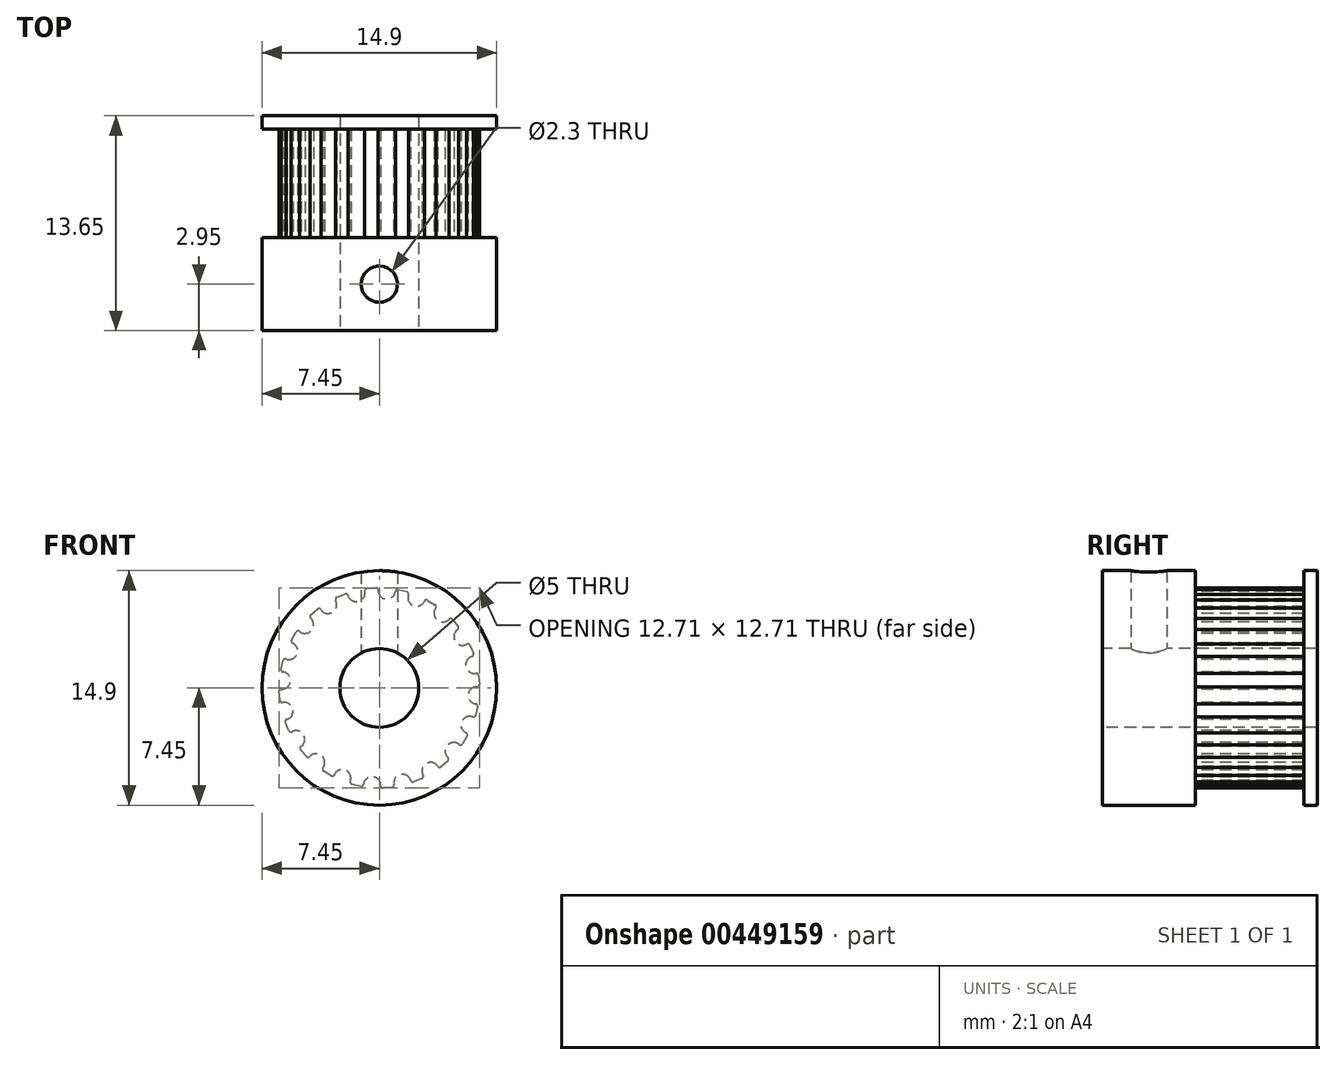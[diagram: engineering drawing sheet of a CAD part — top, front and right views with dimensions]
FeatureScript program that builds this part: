
annotation { "Feature Type Name" : "Feature", "Feature Type Description" : "" }
export const myFeature = defineFeature(function(context is Context, id is Id, definition is map)
    precondition{}
    {
        {
            var Q0;
            Q0=qCreatedBy(makeId("Front.planeOp"),FACE);
            var sketch = newSketch(context, id + "F0", { "sketchPlane" : qUnion([Q0])});
            skLineSegment(sketch, "E0", {"start": v(0, 0) * mm, "end": v(2.42, 5.89) * mm, "construction": true});
            skArc(sketch, "E1", {"start": v(0.43, 5.64) * mm, "mid": v(0.82, 5.76) * mm, "end": v(1.02, 6.12) * mm});
            skArc(sketch, "E2", {"start": v(1.84, 5.93) * mm, "mid": v(1.86, 5.52) * mm, "end": v(2.15, 5.23) * mm});
            skLineSegment(sketch, "E3", {"start": v(1.02, 6.13) * mm, "end": v(1.02, 6.12) * mm});
            skLineSegment(sketch, "E4", {"start": v(1.84, 5.94) * mm, "end": v(1.84, 5.93) * mm});
            skLineSegment(sketch, "E5", {"start": v(1.19, 6.25) * mm, "end": v(1.74, 6.11) * mm});
            skArc(sketch, "E6.filletArc", {"start": v(1.19, 6.25) * mm, "mid": v(1.08, 6.23) * mm, "end": v(1.02, 6.13) * mm});
            skArc(sketch, "E7.filletArc", {"start": v(1.84, 5.94) * mm, "mid": v(1.83, 6.05) * mm, "end": v(1.74, 6.11) * mm});
            skArc(sketch, "E8.1.0", {"start": v(-1.34, 5.5) * mm, "mid": v(-1, 5.73) * mm, "end": v(-0.93, 6.14) * mm});
            skArc(sketch, "E8.1.1", {"start": v(-0.8, 6.3) * mm, "mid": v(-0.9, 6.25) * mm, "end": v(-0.93, 6.15) * mm});
            skLineSegment(sketch, "E8.1.2", {"start": v(-0.8, 6.3) * mm, "end": v(-0.23, 6.35) * mm});
            skLineSegment(sketch, "E8.1.3", {"start": v(-0.93, 6.15) * mm, "end": v(-0.93, 6.14) * mm});
            skArc(sketch, "E8.1.4", {"start": v(-0.08, 6.22) * mm, "mid": v(-0.13, 6.32) * mm, "end": v(-0.23, 6.35) * mm});
            skLineSegment(sketch, "E8.1.5", {"start": v(-0.08, 6.22) * mm, "end": v(-0.08, 6.2) * mm});
            skArc(sketch, "E8.1.6", {"start": v(-0.08, 6.2) * mm, "mid": v(0.06, 5.82) * mm, "end": v(0.43, 5.64) * mm});
            skArc(sketch, "E8.2.0", {"start": v(-2.97, 4.81) * mm, "mid": v(-2.73, 5.14) * mm, "end": v(-2.78, 5.55) * mm});
            skArc(sketch, "E8.2.1", {"start": v(-2.71, 5.75) * mm, "mid": v(-2.79, 5.67) * mm, "end": v(-2.78, 5.56) * mm});
            skLineSegment(sketch, "E8.2.2", {"start": v(-2.71, 5.75) * mm, "end": v(-2.18, 5.97) * mm});
            skLineSegment(sketch, "E8.2.3", {"start": v(-2.78, 5.56) * mm, "end": v(-2.78, 5.55) * mm});
            skArc(sketch, "E8.2.4", {"start": v(-2, 5.89) * mm, "mid": v(-2.07, 5.97) * mm, "end": v(-2.18, 5.97) * mm});
            skLineSegment(sketch, "E8.2.5", {"start": v(-2, 5.89) * mm, "end": v(-2, 5.88) * mm});
            skArc(sketch, "E8.2.6", {"start": v(-2, 5.88) * mm, "mid": v(-1.74, 5.55) * mm, "end": v(-1.34, 5.5) * mm});
            skArc(sketch, "E8.3.0", {"start": v(-4.31, 3.66) * mm, "mid": v(-4.18, 4.05) * mm, "end": v(-4.36, 4.42) * mm});
            skArc(sketch, "E8.3.1", {"start": v(-4.35, 4.63) * mm, "mid": v(-4.4, 4.53) * mm, "end": v(-4.36, 4.43) * mm});
            skLineSegment(sketch, "E8.3.2", {"start": v(-4.35, 4.63) * mm, "end": v(-3.92, 5) * mm});
            skLineSegment(sketch, "E8.3.3", {"start": v(-4.36, 4.43) * mm, "end": v(-4.36, 4.42) * mm});
            skArc(sketch, "E8.3.4", {"start": v(-3.72, 4.98) * mm, "mid": v(-3.82, 5.04) * mm, "end": v(-3.92, 5) * mm});
            skLineSegment(sketch, "E8.3.5", {"start": v(-3.72, 4.98) * mm, "end": v(-3.71, 4.97) * mm});
            skArc(sketch, "E8.3.6", {"start": v(-3.71, 4.97) * mm, "mid": v(-3.37, 4.74) * mm, "end": v(-2.97, 4.81) * mm});
            skArc(sketch, "E8.4.0", {"start": v(-5.23, 2.15) * mm, "mid": v(-5.23, 2.56) * mm, "end": v(-5.5, 2.86) * mm});
            skArc(sketch, "E8.4.1", {"start": v(-5.57, 3.06) * mm, "mid": v(-5.59, 2.95) * mm, "end": v(-5.52, 2.86) * mm});
            skLineSegment(sketch, "E8.4.2", {"start": v(-5.57, 3.06) * mm, "end": v(-5.28, 3.55) * mm});
            skLineSegment(sketch, "E8.4.3", {"start": v(-5.52, 2.86) * mm, "end": v(-5.5, 2.86) * mm});
            skArc(sketch, "E8.4.4", {"start": v(-5.08, 3.59) * mm, "mid": v(-5.19, 3.61) * mm, "end": v(-5.28, 3.55) * mm});
            skLineSegment(sketch, "E8.4.5", {"start": v(-5.08, 3.59) * mm, "end": v(-5.07, 3.58) * mm});
            skArc(sketch, "E8.4.6", {"start": v(-5.07, 3.58) * mm, "mid": v(-4.67, 3.47) * mm, "end": v(-4.31, 3.66) * mm});
            skArc(sketch, "E8.5.0", {"start": v(-5.64, 0.43) * mm, "mid": v(-5.76, 0.82) * mm, "end": v(-6.12, 1.02) * mm});
            skArc(sketch, "E8.5.1", {"start": v(-6.25, 1.19) * mm, "mid": v(-6.23, 1.08) * mm, "end": v(-6.13, 1.02) * mm});
            skLineSegment(sketch, "E8.5.2", {"start": v(-6.25, 1.19) * mm, "end": v(-6.11, 1.74) * mm});
            skLineSegment(sketch, "E8.5.3", {"start": v(-6.13, 1.02) * mm, "end": v(-6.12, 1.02) * mm});
            skArc(sketch, "E8.5.4", {"start": v(-5.94, 1.84) * mm, "mid": v(-6.05, 1.83) * mm, "end": v(-6.11, 1.74) * mm});
            skLineSegment(sketch, "E8.5.5", {"start": v(-5.94, 1.84) * mm, "end": v(-5.93, 1.84) * mm});
            skArc(sketch, "E8.5.6", {"start": v(-5.93, 1.84) * mm, "mid": v(-5.52, 1.86) * mm, "end": v(-5.23, 2.15) * mm});
            skArc(sketch, "E8.6.0", {"start": v(-5.5, -1.34) * mm, "mid": v(-5.73, -1) * mm, "end": v(-6.14, -0.93) * mm});
            skArc(sketch, "E8.6.1", {"start": v(-6.3, -0.8) * mm, "mid": v(-6.25, -0.9) * mm, "end": v(-6.15, -0.93) * mm});
            skLineSegment(sketch, "E8.6.2", {"start": v(-6.3, -0.8) * mm, "end": v(-6.35, -0.23) * mm});
            skLineSegment(sketch, "E8.6.3", {"start": v(-6.15, -0.93) * mm, "end": v(-6.14, -0.93) * mm});
            skArc(sketch, "E8.6.4", {"start": v(-6.22, -0.08) * mm, "mid": v(-6.32, -0.13) * mm, "end": v(-6.35, -0.23) * mm});
            skLineSegment(sketch, "E8.6.5", {"start": v(-6.22, -0.08) * mm, "end": v(-6.2, -0.08) * mm});
            skArc(sketch, "E8.6.6", {"start": v(-6.2, -0.08) * mm, "mid": v(-5.82, 0.06) * mm, "end": v(-5.64, 0.43) * mm});
            skArc(sketch, "E8.7.0", {"start": v(-4.81, -2.97) * mm, "mid": v(-5.14, -2.73) * mm, "end": v(-5.55, -2.78) * mm});
            skArc(sketch, "E8.7.1", {"start": v(-5.75, -2.71) * mm, "mid": v(-5.67, -2.79) * mm, "end": v(-5.56, -2.78) * mm});
            skLineSegment(sketch, "E8.7.2", {"start": v(-5.75, -2.71) * mm, "end": v(-5.97, -2.18) * mm});
            skLineSegment(sketch, "E8.7.3", {"start": v(-5.56, -2.78) * mm, "end": v(-5.55, -2.78) * mm});
            skArc(sketch, "E8.7.4", {"start": v(-5.89, -2) * mm, "mid": v(-5.97, -2.07) * mm, "end": v(-5.97, -2.18) * mm});
            skLineSegment(sketch, "E8.7.5", {"start": v(-5.89, -2) * mm, "end": v(-5.88, -2) * mm});
            skArc(sketch, "E8.7.6", {"start": v(-5.88, -2) * mm, "mid": v(-5.55, -1.74) * mm, "end": v(-5.5, -1.34) * mm});
            skArc(sketch, "E8.8.0", {"start": v(-3.66, -4.31) * mm, "mid": v(-4.05, -4.18) * mm, "end": v(-4.42, -4.36) * mm});
            skArc(sketch, "E8.8.1", {"start": v(-4.63, -4.35) * mm, "mid": v(-4.53, -4.4) * mm, "end": v(-4.43, -4.36) * mm});
            skLineSegment(sketch, "E8.8.2", {"start": v(-4.63, -4.35) * mm, "end": v(-5, -3.92) * mm});
            skLineSegment(sketch, "E8.8.3", {"start": v(-4.43, -4.36) * mm, "end": v(-4.42, -4.36) * mm});
            skArc(sketch, "E8.8.4", {"start": v(-4.98, -3.72) * mm, "mid": v(-5.04, -3.82) * mm, "end": v(-5, -3.92) * mm});
            skLineSegment(sketch, "E8.8.5", {"start": v(-4.98, -3.72) * mm, "end": v(-4.97, -3.71) * mm});
            skArc(sketch, "E8.8.6", {"start": v(-4.97, -3.71) * mm, "mid": v(-4.74, -3.37) * mm, "end": v(-4.81, -2.97) * mm});
            skArc(sketch, "E8.9.0", {"start": v(-2.15, -5.23) * mm, "mid": v(-2.56, -5.23) * mm, "end": v(-2.86, -5.5) * mm});
            skArc(sketch, "E8.9.1", {"start": v(-3.06, -5.57) * mm, "mid": v(-2.95, -5.59) * mm, "end": v(-2.86, -5.52) * mm});
            skLineSegment(sketch, "E8.9.2", {"start": v(-3.06, -5.57) * mm, "end": v(-3.55, -5.28) * mm});
            skLineSegment(sketch, "E8.9.3", {"start": v(-2.86, -5.52) * mm, "end": v(-2.86, -5.5) * mm});
            skArc(sketch, "E8.9.4", {"start": v(-3.59, -5.08) * mm, "mid": v(-3.61, -5.19) * mm, "end": v(-3.55, -5.28) * mm});
            skLineSegment(sketch, "E8.9.5", {"start": v(-3.59, -5.08) * mm, "end": v(-3.58, -5.07) * mm});
            skArc(sketch, "E8.9.6", {"start": v(-3.58, -5.07) * mm, "mid": v(-3.47, -4.67) * mm, "end": v(-3.66, -4.31) * mm});
            skArc(sketch, "E8.10.0", {"start": v(-0.43, -5.64) * mm, "mid": v(-0.82, -5.76) * mm, "end": v(-1.02, -6.12) * mm});
            skArc(sketch, "E8.10.1", {"start": v(-1.19, -6.25) * mm, "mid": v(-1.08, -6.23) * mm, "end": v(-1.02, -6.13) * mm});
            skLineSegment(sketch, "E8.10.2", {"start": v(-1.19, -6.25) * mm, "end": v(-1.74, -6.11) * mm});
            skLineSegment(sketch, "E8.10.3", {"start": v(-1.02, -6.13) * mm, "end": v(-1.02, -6.12) * mm});
            skArc(sketch, "E8.10.4", {"start": v(-1.84, -5.94) * mm, "mid": v(-1.83, -6.05) * mm, "end": v(-1.74, -6.11) * mm});
            skLineSegment(sketch, "E8.10.5", {"start": v(-1.84, -5.94) * mm, "end": v(-1.84, -5.93) * mm});
            skArc(sketch, "E8.10.6", {"start": v(-1.84, -5.93) * mm, "mid": v(-1.86, -5.52) * mm, "end": v(-2.15, -5.23) * mm});
            skArc(sketch, "E8.11.0", {"start": v(1.34, -5.5) * mm, "mid": v(1, -5.73) * mm, "end": v(0.93, -6.14) * mm});
            skArc(sketch, "E8.11.1", {"start": v(0.8, -6.3) * mm, "mid": v(0.9, -6.25) * mm, "end": v(0.93, -6.15) * mm});
            skLineSegment(sketch, "E8.11.2", {"start": v(0.8, -6.3) * mm, "end": v(0.23, -6.35) * mm});
            skLineSegment(sketch, "E8.11.3", {"start": v(0.93, -6.15) * mm, "end": v(0.93, -6.14) * mm});
            skArc(sketch, "E8.11.4", {"start": v(0.08, -6.22) * mm, "mid": v(0.13, -6.32) * mm, "end": v(0.23, -6.35) * mm});
            skLineSegment(sketch, "E8.11.5", {"start": v(0.08, -6.22) * mm, "end": v(0.08, -6.2) * mm});
            skArc(sketch, "E8.11.6", {"start": v(0.08, -6.2) * mm, "mid": v(-0.06, -5.82) * mm, "end": v(-0.43, -5.64) * mm});
            skArc(sketch, "E8.12.0", {"start": v(2.97, -4.81) * mm, "mid": v(2.73, -5.14) * mm, "end": v(2.78, -5.55) * mm});
            skArc(sketch, "E8.12.1", {"start": v(2.71, -5.75) * mm, "mid": v(2.79, -5.67) * mm, "end": v(2.78, -5.56) * mm});
            skLineSegment(sketch, "E8.12.2", {"start": v(2.71, -5.75) * mm, "end": v(2.18, -5.97) * mm});
            skLineSegment(sketch, "E8.12.3", {"start": v(2.78, -5.56) * mm, "end": v(2.78, -5.55) * mm});
            skArc(sketch, "E8.12.4", {"start": v(2, -5.89) * mm, "mid": v(2.07, -5.97) * mm, "end": v(2.18, -5.97) * mm});
            skLineSegment(sketch, "E8.12.5", {"start": v(2, -5.89) * mm, "end": v(2, -5.88) * mm});
            skArc(sketch, "E8.12.6", {"start": v(2, -5.88) * mm, "mid": v(1.74, -5.55) * mm, "end": v(1.34, -5.5) * mm});
            skArc(sketch, "E8.13.0", {"start": v(4.31, -3.66) * mm, "mid": v(4.18, -4.05) * mm, "end": v(4.36, -4.42) * mm});
            skArc(sketch, "E8.13.1", {"start": v(4.35, -4.63) * mm, "mid": v(4.4, -4.53) * mm, "end": v(4.36, -4.43) * mm});
            skLineSegment(sketch, "E8.13.2", {"start": v(4.35, -4.63) * mm, "end": v(3.92, -5) * mm});
            skLineSegment(sketch, "E8.13.3", {"start": v(4.36, -4.43) * mm, "end": v(4.36, -4.42) * mm});
            skArc(sketch, "E8.13.4", {"start": v(3.72, -4.98) * mm, "mid": v(3.82, -5.04) * mm, "end": v(3.92, -5) * mm});
            skLineSegment(sketch, "E8.13.5", {"start": v(3.72, -4.98) * mm, "end": v(3.71, -4.97) * mm});
            skArc(sketch, "E8.13.6", {"start": v(3.71, -4.97) * mm, "mid": v(3.37, -4.74) * mm, "end": v(2.97, -4.81) * mm});
            skArc(sketch, "E8.14.0", {"start": v(5.23, -2.15) * mm, "mid": v(5.23, -2.56) * mm, "end": v(5.5, -2.86) * mm});
            skArc(sketch, "E8.14.1", {"start": v(5.57, -3.06) * mm, "mid": v(5.59, -2.95) * mm, "end": v(5.52, -2.86) * mm});
            skLineSegment(sketch, "E8.14.2", {"start": v(5.57, -3.06) * mm, "end": v(5.28, -3.55) * mm});
            skLineSegment(sketch, "E8.14.3", {"start": v(5.52, -2.86) * mm, "end": v(5.5, -2.86) * mm});
            skArc(sketch, "E8.14.4", {"start": v(5.08, -3.59) * mm, "mid": v(5.19, -3.61) * mm, "end": v(5.28, -3.55) * mm});
            skLineSegment(sketch, "E8.14.5", {"start": v(5.08, -3.59) * mm, "end": v(5.07, -3.58) * mm});
            skArc(sketch, "E8.14.6", {"start": v(5.07, -3.58) * mm, "mid": v(4.67, -3.47) * mm, "end": v(4.31, -3.66) * mm});
            skArc(sketch, "E8.15.0", {"start": v(5.64, -0.43) * mm, "mid": v(5.76, -0.82) * mm, "end": v(6.12, -1.02) * mm});
            skArc(sketch, "E8.15.1", {"start": v(6.25, -1.19) * mm, "mid": v(6.23, -1.08) * mm, "end": v(6.13, -1.02) * mm});
            skLineSegment(sketch, "E8.15.2", {"start": v(6.25, -1.19) * mm, "end": v(6.11, -1.74) * mm});
            skLineSegment(sketch, "E8.15.3", {"start": v(6.13, -1.02) * mm, "end": v(6.12, -1.02) * mm});
            skArc(sketch, "E8.15.4", {"start": v(5.94, -1.84) * mm, "mid": v(6.05, -1.83) * mm, "end": v(6.11, -1.74) * mm});
            skLineSegment(sketch, "E8.15.5", {"start": v(5.94, -1.84) * mm, "end": v(5.93, -1.84) * mm});
            skArc(sketch, "E8.15.6", {"start": v(5.93, -1.84) * mm, "mid": v(5.52, -1.86) * mm, "end": v(5.23, -2.15) * mm});
            skArc(sketch, "E8.16.0", {"start": v(5.5, 1.34) * mm, "mid": v(5.73, 1) * mm, "end": v(6.14, 0.93) * mm});
            skArc(sketch, "E8.16.1", {"start": v(6.3, 0.8) * mm, "mid": v(6.25, 0.9) * mm, "end": v(6.15, 0.93) * mm});
            skLineSegment(sketch, "E8.16.2", {"start": v(6.3, 0.8) * mm, "end": v(6.35, 0.23) * mm});
            skLineSegment(sketch, "E8.16.3", {"start": v(6.15, 0.93) * mm, "end": v(6.14, 0.93) * mm});
            skArc(sketch, "E8.16.4", {"start": v(6.22, 0.08) * mm, "mid": v(6.32, 0.13) * mm, "end": v(6.35, 0.23) * mm});
            skLineSegment(sketch, "E8.16.5", {"start": v(6.22, 0.08) * mm, "end": v(6.2, 0.08) * mm});
            skArc(sketch, "E8.16.6", {"start": v(6.2, 0.08) * mm, "mid": v(5.82, -0.06) * mm, "end": v(5.64, -0.43) * mm});
            skArc(sketch, "E8.17.0", {"start": v(4.81, 2.97) * mm, "mid": v(5.14, 2.73) * mm, "end": v(5.55, 2.78) * mm});
            skArc(sketch, "E8.17.1", {"start": v(5.75, 2.71) * mm, "mid": v(5.67, 2.79) * mm, "end": v(5.56, 2.78) * mm});
            skLineSegment(sketch, "E8.17.2", {"start": v(5.75, 2.71) * mm, "end": v(5.97, 2.18) * mm});
            skLineSegment(sketch, "E8.17.3", {"start": v(5.56, 2.78) * mm, "end": v(5.55, 2.78) * mm});
            skArc(sketch, "E8.17.4", {"start": v(5.89, 2) * mm, "mid": v(5.97, 2.07) * mm, "end": v(5.97, 2.18) * mm});
            skLineSegment(sketch, "E8.17.5", {"start": v(5.89, 2) * mm, "end": v(5.88, 2) * mm});
            skArc(sketch, "E8.17.6", {"start": v(5.88, 2) * mm, "mid": v(5.55, 1.74) * mm, "end": v(5.5, 1.34) * mm});
            skArc(sketch, "E8.18.0", {"start": v(3.66, 4.31) * mm, "mid": v(4.05, 4.18) * mm, "end": v(4.42, 4.36) * mm});
            skArc(sketch, "E8.18.1", {"start": v(4.63, 4.35) * mm, "mid": v(4.53, 4.4) * mm, "end": v(4.43, 4.36) * mm});
            skLineSegment(sketch, "E8.18.2", {"start": v(4.63, 4.35) * mm, "end": v(5, 3.92) * mm});
            skLineSegment(sketch, "E8.18.3", {"start": v(4.43, 4.36) * mm, "end": v(4.42, 4.36) * mm});
            skArc(sketch, "E8.18.4", {"start": v(4.98, 3.72) * mm, "mid": v(5.04, 3.82) * mm, "end": v(5, 3.92) * mm});
            skLineSegment(sketch, "E8.18.5", {"start": v(4.98, 3.72) * mm, "end": v(4.97, 3.71) * mm});
            skArc(sketch, "E8.18.6", {"start": v(4.97, 3.71) * mm, "mid": v(4.74, 3.37) * mm, "end": v(4.81, 2.97) * mm});
            skArc(sketch, "E8.19.0", {"start": v(2.15, 5.23) * mm, "mid": v(2.56, 5.23) * mm, "end": v(2.86, 5.5) * mm});
            skArc(sketch, "E8.19.1", {"start": v(3.06, 5.57) * mm, "mid": v(2.95, 5.59) * mm, "end": v(2.86, 5.52) * mm});
            skLineSegment(sketch, "E8.19.2", {"start": v(3.06, 5.57) * mm, "end": v(3.55, 5.28) * mm});
            skLineSegment(sketch, "E8.19.3", {"start": v(2.86, 5.52) * mm, "end": v(2.86, 5.5) * mm});
            skArc(sketch, "E8.19.4", {"start": v(3.59, 5.08) * mm, "mid": v(3.61, 5.19) * mm, "end": v(3.55, 5.28) * mm});
            skLineSegment(sketch, "E8.19.5", {"start": v(3.59, 5.08) * mm, "end": v(3.58, 5.07) * mm});
            skArc(sketch, "E8.19.6", {"start": v(3.58, 5.07) * mm, "mid": v(3.47, 4.67) * mm, "end": v(3.66, 4.31) * mm});
            skPoint(sketch, "E8.center", {"position": v(0, 0) * mm});
            skCircle(sketch, "E9", {"center": v(0, 0) * mm, "radius": 2.5 * mm});
            skCircle(sketch, "E10", {"center": v(0, 0) * mm, "radius": 7.45 * mm});
            skSolve(sketch);
        }
        {
            var Q0;
            Q0=makeQuery(id+"F0.imprint","IMPRINT",FACE,{"disambiguationData":[TD([[makeQuery(id+"F0.imprint","IMPRINT",EDGE,{"derivedFrom":sQuery(id+"F0.wireOp",EDGE,"E1")}),-1.0]])]});
            extrude(context, id + "F1", {"entities" : qUnion([Q0]), "oppositeDirection" : true, "depth" : 6.9 * mm});
        }
        {
            var Q0;
            Q0=makeQuery(id+"F0.imprint","IMPRINT",FACE,{"disambiguationData":[TD([[makeQuery(id+"F0.imprint","IMPRINT",EDGE,{"derivedFrom":sQuery(id+"F0.wireOp",EDGE,"E1")}),-1.0]])]});
            var Q1;
            Q1=makeQuery(id+"F0.imprint","IMPRINT",FACE,{"disambiguationData":[TD([[makeQuery(id+"F0.imprint","IMPRINT",EDGE,{"derivedFrom":sQuery(id+"F0.wireOp",EDGE,"E1")}),1.0]])]});
            extrude(context, id + "F2", {"entities" : qUnion([Q0, Q1]), "operationType" : NewBodyOperationType.ADD, "depth" : 5.9 * mm});
        }
        {
            var Q0;
            Q0=makeQuery(id+"F1.opExtrude","CAP_FACE",FACE,{"disambiguationData":[OSD([sQuery(id+"F0.wireOp",EDGE,"E1"),sQuery(id+"F0.wireOp",EDGE,"E2"),sQuery(id+"F0.wireOp",EDGE,"E3"),sQuery(id+"F0.wireOp",EDGE,"E4"),sQuery(id+"F0.wireOp",EDGE,"E5"),sQuery(id+"F0.wireOp",EDGE,"E6.filletArc"),sQuery(id+"F0.wireOp",EDGE,"E7.filletArc"),sQuery(id+"F0.wireOp",EDGE,"E8.1.0"),sQuery(id+"F0.wireOp",EDGE,"E8.1.1"),sQuery(id+"F0.wireOp",EDGE,"E8.1.2"),sQuery(id+"F0.wireOp",EDGE,"E8.1.3"),sQuery(id+"F0.wireOp",EDGE,"E8.1.4"),sQuery(id+"F0.wireOp",EDGE,"E8.1.5"),sQuery(id+"F0.wireOp",EDGE,"E8.1.6"),sQuery(id+"F0.wireOp",EDGE,"E8.2.0"),sQuery(id+"F0.wireOp",EDGE,"E8.2.1"),sQuery(id+"F0.wireOp",EDGE,"E8.2.2"),sQuery(id+"F0.wireOp",EDGE,"E8.2.3"),sQuery(id+"F0.wireOp",EDGE,"E8.2.4"),sQuery(id+"F0.wireOp",EDGE,"E8.2.5"),sQuery(id+"F0.wireOp",EDGE,"E8.2.6"),sQuery(id+"F0.wireOp",EDGE,"E8.3.0"),sQuery(id+"F0.wireOp",EDGE,"E8.3.1"),sQuery(id+"F0.wireOp",EDGE,"E8.3.2"),sQuery(id+"F0.wireOp",EDGE,"E8.3.3"),sQuery(id+"F0.wireOp",EDGE,"E8.3.4"),sQuery(id+"F0.wireOp",EDGE,"E8.3.5"),sQuery(id+"F0.wireOp",EDGE,"E8.3.6"),sQuery(id+"F0.wireOp",EDGE,"E8.4.0"),sQuery(id+"F0.wireOp",EDGE,"E8.4.1"),sQuery(id+"F0.wireOp",EDGE,"E8.4.2"),sQuery(id+"F0.wireOp",EDGE,"E8.4.3"),sQuery(id+"F0.wireOp",EDGE,"E8.4.4"),sQuery(id+"F0.wireOp",EDGE,"E8.4.5"),sQuery(id+"F0.wireOp",EDGE,"E8.4.6"),sQuery(id+"F0.wireOp",EDGE,"E8.5.0"),sQuery(id+"F0.wireOp",EDGE,"E8.5.1"),sQuery(id+"F0.wireOp",EDGE,"E8.5.2"),sQuery(id+"F0.wireOp",EDGE,"E8.5.3"),sQuery(id+"F0.wireOp",EDGE,"E8.5.4"),sQuery(id+"F0.wireOp",EDGE,"E8.5.5"),sQuery(id+"F0.wireOp",EDGE,"E8.5.6"),sQuery(id+"F0.wireOp",EDGE,"E8.6.0"),sQuery(id+"F0.wireOp",EDGE,"E8.6.1"),sQuery(id+"F0.wireOp",EDGE,"E8.6.2"),sQuery(id+"F0.wireOp",EDGE,"E8.6.3"),sQuery(id+"F0.wireOp",EDGE,"E8.6.4"),sQuery(id+"F0.wireOp",EDGE,"E8.6.5"),sQuery(id+"F0.wireOp",EDGE,"E8.6.6"),sQuery(id+"F0.wireOp",EDGE,"E8.7.0"),sQuery(id+"F0.wireOp",EDGE,"E8.7.1"),sQuery(id+"F0.wireOp",EDGE,"E8.7.2"),sQuery(id+"F0.wireOp",EDGE,"E8.7.3"),sQuery(id+"F0.wireOp",EDGE,"E8.7.4"),sQuery(id+"F0.wireOp",EDGE,"E8.7.5"),sQuery(id+"F0.wireOp",EDGE,"E8.7.6"),sQuery(id+"F0.wireOp",EDGE,"E8.8.0"),sQuery(id+"F0.wireOp",EDGE,"E8.8.1"),sQuery(id+"F0.wireOp",EDGE,"E8.8.2"),sQuery(id+"F0.wireOp",EDGE,"E8.8.3"),sQuery(id+"F0.wireOp",EDGE,"E8.8.4"),sQuery(id+"F0.wireOp",EDGE,"E8.8.5"),sQuery(id+"F0.wireOp",EDGE,"E8.8.6"),sQuery(id+"F0.wireOp",EDGE,"E8.9.0"),sQuery(id+"F0.wireOp",EDGE,"E8.9.1"),sQuery(id+"F0.wireOp",EDGE,"E8.9.2"),sQuery(id+"F0.wireOp",EDGE,"E8.9.3"),sQuery(id+"F0.wireOp",EDGE,"E8.9.4"),sQuery(id+"F0.wireOp",EDGE,"E8.9.5"),sQuery(id+"F0.wireOp",EDGE,"E8.9.6"),sQuery(id+"F0.wireOp",EDGE,"E8.10.0"),sQuery(id+"F0.wireOp",EDGE,"E8.10.1"),sQuery(id+"F0.wireOp",EDGE,"E8.10.2"),sQuery(id+"F0.wireOp",EDGE,"E8.10.3"),sQuery(id+"F0.wireOp",EDGE,"E8.10.4"),sQuery(id+"F0.wireOp",EDGE,"E8.10.5"),sQuery(id+"F0.wireOp",EDGE,"E8.10.6"),sQuery(id+"F0.wireOp",EDGE,"E8.11.0"),sQuery(id+"F0.wireOp",EDGE,"E8.11.1"),sQuery(id+"F0.wireOp",EDGE,"E8.11.2"),sQuery(id+"F0.wireOp",EDGE,"E8.11.3"),sQuery(id+"F0.wireOp",EDGE,"E8.11.4"),sQuery(id+"F0.wireOp",EDGE,"E8.11.5"),sQuery(id+"F0.wireOp",EDGE,"E8.11.6"),sQuery(id+"F0.wireOp",EDGE,"E8.12.0"),sQuery(id+"F0.wireOp",EDGE,"E8.12.1"),sQuery(id+"F0.wireOp",EDGE,"E8.12.2"),sQuery(id+"F0.wireOp",EDGE,"E8.12.3"),sQuery(id+"F0.wireOp",EDGE,"E8.12.4"),sQuery(id+"F0.wireOp",EDGE,"E8.12.5"),sQuery(id+"F0.wireOp",EDGE,"E8.12.6"),sQuery(id+"F0.wireOp",EDGE,"E8.13.0"),sQuery(id+"F0.wireOp",EDGE,"E8.13.1"),sQuery(id+"F0.wireOp",EDGE,"E8.13.2"),sQuery(id+"F0.wireOp",EDGE,"E8.13.3"),sQuery(id+"F0.wireOp",EDGE,"E8.13.4"),sQuery(id+"F0.wireOp",EDGE,"E8.13.5"),sQuery(id+"F0.wireOp",EDGE,"E8.13.6"),sQuery(id+"F0.wireOp",EDGE,"E8.14.0"),sQuery(id+"F0.wireOp",EDGE,"E8.14.1"),sQuery(id+"F0.wireOp",EDGE,"E8.14.2"),sQuery(id+"F0.wireOp",EDGE,"E8.14.3"),sQuery(id+"F0.wireOp",EDGE,"E8.14.4"),sQuery(id+"F0.wireOp",EDGE,"E8.14.5"),sQuery(id+"F0.wireOp",EDGE,"E8.14.6"),sQuery(id+"F0.wireOp",EDGE,"E8.15.0"),sQuery(id+"F0.wireOp",EDGE,"E8.15.1"),sQuery(id+"F0.wireOp",EDGE,"E8.15.2"),sQuery(id+"F0.wireOp",EDGE,"E8.15.3"),sQuery(id+"F0.wireOp",EDGE,"E8.15.4"),sQuery(id+"F0.wireOp",EDGE,"E8.15.5"),sQuery(id+"F0.wireOp",EDGE,"E8.15.6"),sQuery(id+"F0.wireOp",EDGE,"E8.16.0"),sQuery(id+"F0.wireOp",EDGE,"E8.16.1"),sQuery(id+"F0.wireOp",EDGE,"E8.16.2"),sQuery(id+"F0.wireOp",EDGE,"E8.16.3"),sQuery(id+"F0.wireOp",EDGE,"E8.16.4"),sQuery(id+"F0.wireOp",EDGE,"E8.16.5"),sQuery(id+"F0.wireOp",EDGE,"E8.16.6"),sQuery(id+"F0.wireOp",EDGE,"E8.17.0"),sQuery(id+"F0.wireOp",EDGE,"E8.17.1"),sQuery(id+"F0.wireOp",EDGE,"E8.17.2"),sQuery(id+"F0.wireOp",EDGE,"E8.17.3"),sQuery(id+"F0.wireOp",EDGE,"E8.17.4"),sQuery(id+"F0.wireOp",EDGE,"E8.17.5"),sQuery(id+"F0.wireOp",EDGE,"E8.17.6"),sQuery(id+"F0.wireOp",EDGE,"E8.18.0"),sQuery(id+"F0.wireOp",EDGE,"E8.18.1"),sQuery(id+"F0.wireOp",EDGE,"E8.18.2"),sQuery(id+"F0.wireOp",EDGE,"E8.18.3"),sQuery(id+"F0.wireOp",EDGE,"E8.18.4"),sQuery(id+"F0.wireOp",EDGE,"E8.18.5"),sQuery(id+"F0.wireOp",EDGE,"E8.18.6"),sQuery(id+"F0.wireOp",EDGE,"E8.19.0"),sQuery(id+"F0.wireOp",EDGE,"E8.19.1"),sQuery(id+"F0.wireOp",EDGE,"E8.19.2"),sQuery(id+"F0.wireOp",EDGE,"E8.19.3"),sQuery(id+"F0.wireOp",EDGE,"E8.19.4"),sQuery(id+"F0.wireOp",EDGE,"E8.19.5"),sQuery(id+"F0.wireOp",EDGE,"E8.19.6"),sQuery(id+"F0.wireOp",EDGE,"E9")])],"isStart":false});
            var sketch = newSketch(context, id + "F3", { "sketchPlane" : qUnion([Q0])});
            skCircle(sketch, "E11.0", {"center": v(0, 0) * mm, "radius": 7.45 * mm});
            skCircle(sketch, "E12.0", {"center": v(0, 0) * mm, "radius": 2.5 * mm});
            skSolve(sketch);
        }
        {
            var Q0;
            Q0=qSketchRegion(id+"F3",true);
            extrude(context, id + "F4", {"entities" : qUnion([Q0]), "operationType" : NewBodyOperationType.ADD, "depth" : .85 * mm});
        }
        {
            var Q0;
            Q0=qCreatedBy(makeId("Top.planeOp"),FACE);
            var sketch = newSketch(context, id + "F5", { "sketchPlane" : qUnion([Q0])});
            skLineSegment(sketch, "E13.0", {"start": v(2.5, -5.9) * mm, "end": v(-2.5, -5.9) * mm, "construction": true});
            skLineSegment(sketch, "E14.0.0", {"start": v(2.5, 0) * mm, "end": v(-2.5, 0) * mm, "construction": true});
            skLineSegment(sketch, "E15", {"start": v(0, -5.9) * mm, "end": v(0, 0) * mm, "construction": true});
            skCircle(sketch, "E16", {"center": v(0, -2.95) * mm, "radius": 1.15 * mm});
            skSolve(sketch);
        }
        {
            var Q0;
            Q0=makeQuery(id+"F5.imprint","IMPRINT",FACE,{"disambiguationData":[TD([[makeQuery(id+"F5.imprint","IMPRINT",EDGE,{"derivedFrom":sQuery(id+"F5.wireOp",EDGE,"E16")}),1.0]])]});
            extrude(context, id + "F6", {"entities" : qUnion([Q0]), "operationType" : NewBodyOperationType.REMOVE, "depth" : 10 * mm});
        }
    });
